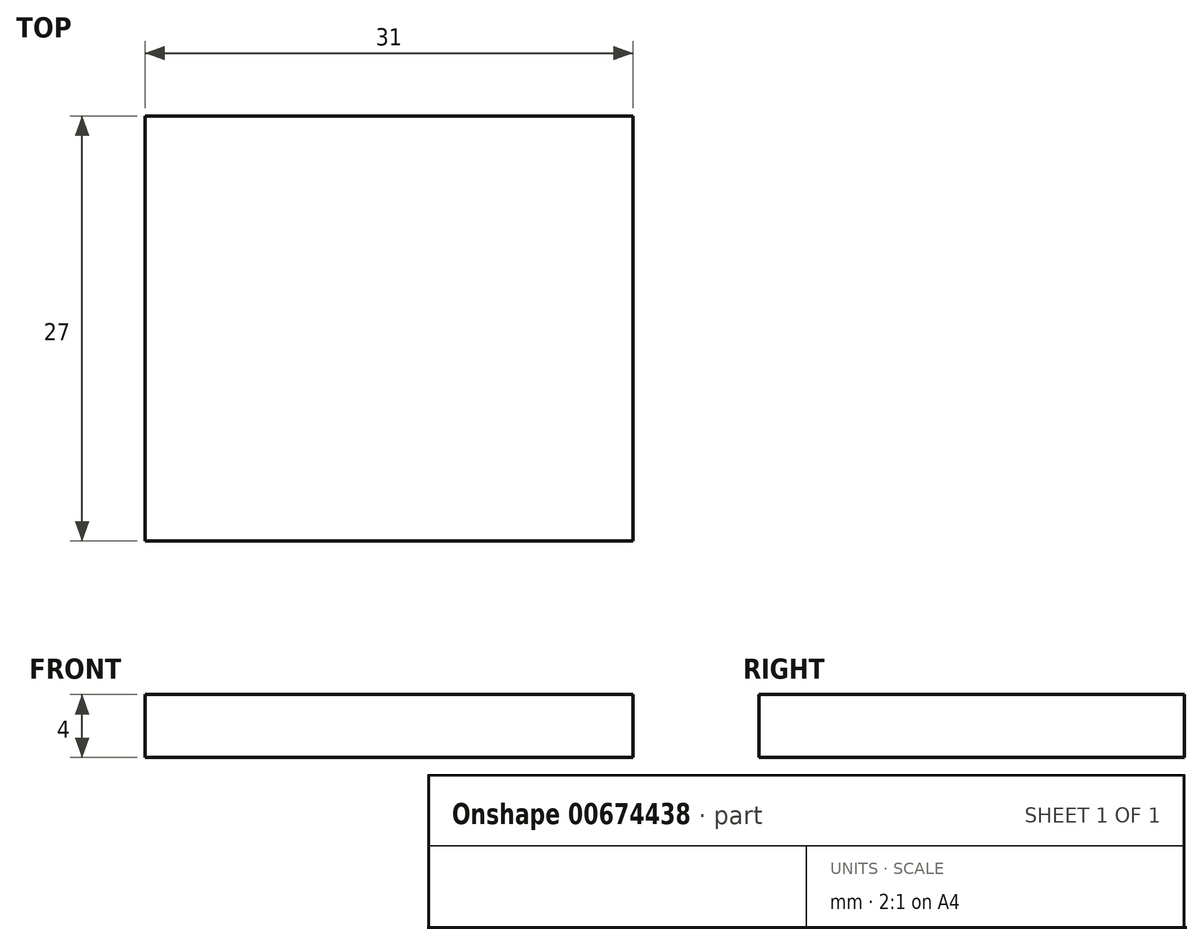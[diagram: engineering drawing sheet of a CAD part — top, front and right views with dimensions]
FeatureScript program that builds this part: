
annotation { "Feature Type Name" : "Feature", "Feature Type Description" : "" }
export const myFeature = defineFeature(function(context is Context, id is Id, definition is map)
    precondition{}
    {
        {
            var Q0;
            Q0=qCreatedBy(makeId("Top.planeOp"),FACE);
            var sketch = newSketch(context, id + "F0", { "sketchPlane" : qUnion([Q0])});
            skLineSegment(sketch, "E0.bottom", {"start": v(0, 0) * mm, "end": v(-31, 0) * mm});
            skLineSegment(sketch, "E0.top", {"start": v(0, 27) * mm, "end": v(-31, 27) * mm});
            skLineSegment(sketch, "E0.left", {"start": v(0, 0) * mm, "end": v(0, 27) * mm});
            skLineSegment(sketch, "E0.right", {"start": v(-31, 0) * mm, "end": v(-31, 27) * mm});
            skSolve(sketch);
        }
        {
            var Q0;
            Q0=makeQuery(id+"F0.imprint","IMPRINT",FACE,{"disambiguationData":[TD([[makeQuery(id+"F0.imprint","IMPRINT",EDGE,{"derivedFrom":sQuery(id+"F0.wireOp",EDGE,"E0.bottom")}),-1.0]])]});
            extrude(context, id + "F1", {"entities" : qUnion([Q0]), "depth" : 4 * mm, "offsetDistance" : 25.4 * mm});
        }
    });
